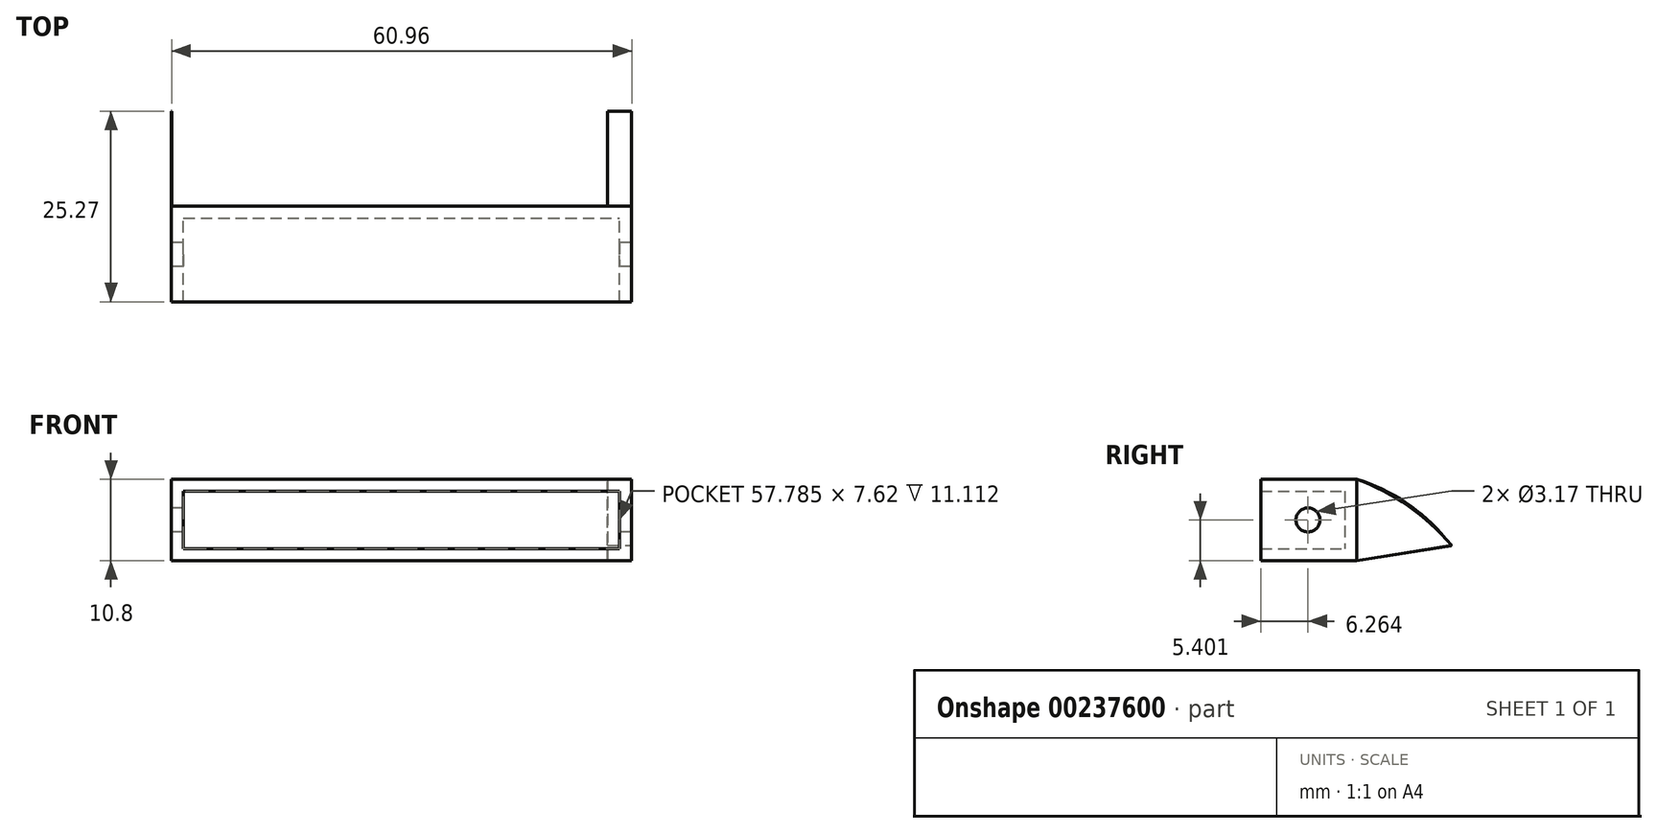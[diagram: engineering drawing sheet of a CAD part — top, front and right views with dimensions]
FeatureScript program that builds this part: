
annotation { "Feature Type Name" : "Feature", "Feature Type Description" : "" }
export const myFeature = defineFeature(function(context is Context, id is Id, definition is map)
    precondition{}
    {
        {
            var Q0;
            Q0=qCreatedBy(makeId("Front.planeOp"),FACE);
            var sketch = newSketch(context, id + "F0", { "sketchPlane" : qUnion([Q0])});
            skLineSegment(sketch, "E0.bottom", {"start": v(-19.84, 6.8) * mm, "end": v(41.12, 6.8) * mm});
            skLineSegment(sketch, "E0.top", {"start": v(-19.84, -4) * mm, "end": v(41.12, -4) * mm});
            skLineSegment(sketch, "E0.left", {"start": v(-19.84, 6.8) * mm, "end": v(-19.84, -4) * mm});
            skLineSegment(sketch, "E0.right", {"start": v(41.12, 6.8) * mm, "end": v(41.12, -4) * mm});
            skSolve(sketch);
        }
        {
            var Q0;
            Q0=makeQuery(id+"F0.imprint","IMPRINT",FACE,{"disambiguationData":[TD([[makeQuery(id+"F0.imprint","IMPRINT",EDGE,{"derivedFrom":sQuery(id+"F0.wireOp",EDGE,"E0.bottom")}),-1.0]])]});
            extrude(context, id + "F1", {"entities" : qUnion([Q0]), "depth" : 12.7 * mm});
        }
        {
            var Q0;
            Q0=makeQuery(id+"F1.opExtrude","CAP_FACE",FACE,{"disambiguationData":[OSD([sQuery(id+"F0.wireOp",EDGE,"E0.bottom"),sQuery(id+"F0.wireOp",EDGE,"E0.top"),sQuery(id+"F0.wireOp",EDGE,"E0.left"),sQuery(id+"F0.wireOp",EDGE,"E0.right")])],"isStart":false});
            shell(context, id + "F2", {"entities" : qUnion([Q0]), "thickness" : 1.59 * mm});
        }
        {
            var Q0;
            Q0=makeQuery(id+"F1.opExtrude","SWEPT_FACE",FACE,{"disambiguationData":[OSD([sQuery(id+"F0.wireOp",EDGE,"E0.left")])]});
            var sketch = newSketch(context, id + "F3", { "sketchPlane" : qUnion([Q0])});
            skCircle(sketch, "E1", {"center": v(6.44, 1.4) * mm, "radius": 1.59 * mm});
            skSolve(sketch);
        }
        {
            var Q0;
            Q0=sQuery(id+"F3.wireOp",VERTEX,"E1.center");
            var Q1;
            Q1=makeQuery(id+"F1.opExtrude","SWEPT_BODY",BODY,{"disambiguationData":[OSD([sQuery(id+"F0.wireOp",EDGE,"E0.bottom"),sQuery(id+"F0.wireOp",EDGE,"E0.top"),sQuery(id+"F0.wireOp",EDGE,"E0.left"),sQuery(id+"F0.wireOp",EDGE,"E0.right")])]});
            hole(context, id + "F4", {"style" : HoleStyle.C_SINK, "endStyle" : HoleEndStyle.BLIND, "holeDiameter" : 3.17 * mm, "cSinkDiameter" : 3.17 * mm, "cSinkAngle" : 90 * degree, "holeDepth" : 76.2 * mm, "startFromSketch" : true, "locations" : qUnion([Q0]), "scope" : qUnion([Q1])});
        }
        {
            var Q0;
            Q0=makeQuery(id+"F1.opExtrude","SWEPT_FACE",FACE,{"disambiguationData":[OSD([sQuery(id+"F0.wireOp",EDGE,"E0.left")])]});
            var sketch = newSketch(context, id + "F5", { "sketchPlane" : qUnion([Q0])});
            skLineSegment(sketch, "E2", {"start": v(0, -4) * mm, "end": v(-12.55, -2.03) * mm});
            skArc(sketch, "E3", {"start": v(0, 6.8) * mm, "mid": v(-6.98, 3.39) * mm, "end": v(-12.55, -2.03) * mm});
            skSolve(sketch);
        }
        {
            var Q0;
            Q0=makeQuery(id+"F5.imprint","IMPRINT",FACE,{"disambiguationData":[TD([[makeQuery(id+"F5.imprint","IMPRINT",EDGE,{"derivedFrom":sQuery(id+"F5.wireOp",EDGE,"E2")}),-1.0]])]});
            extrude(context, id + "F6", {"entities" : qUnion([Q0]), "oppositeDirection" : true, "depth" : 1 / 203.2 * mm});
        }
        {
            var Q0;
            Q0=makeQuery(id+"F1.opExtrude","SWEPT_FACE",FACE,{"disambiguationData":[OSD([sQuery(id+"F0.wireOp",EDGE,"E0.right")])]});
            var sketch = newSketch(context, id + "F7", { "sketchPlane" : qUnion([Q0])});
            skLineSegment(sketch, "E4", {"start": v(0, -4) * mm, "end": v(12.57, -1.95) * mm});
            skArc(sketch, "E5", {"start": v(12.57, -1.95) * mm, "mid": v(6.85, 3.24) * mm, "end": v(0, 6.8) * mm});
            skLineSegment(sketch, "E6", {"start": v(0, 6.8) * mm, "end": v(0, -4) * mm});
            skSolve(sketch);
        }
        {
            var Q0;
            Q0 = qSketchRegion(id + "F7", true);
            extrude(context, id + "F8", {"entities" : qUnion([Q0]), "oppositeDirection" : true, "depth" : 3.17 * mm});
        }
    });
